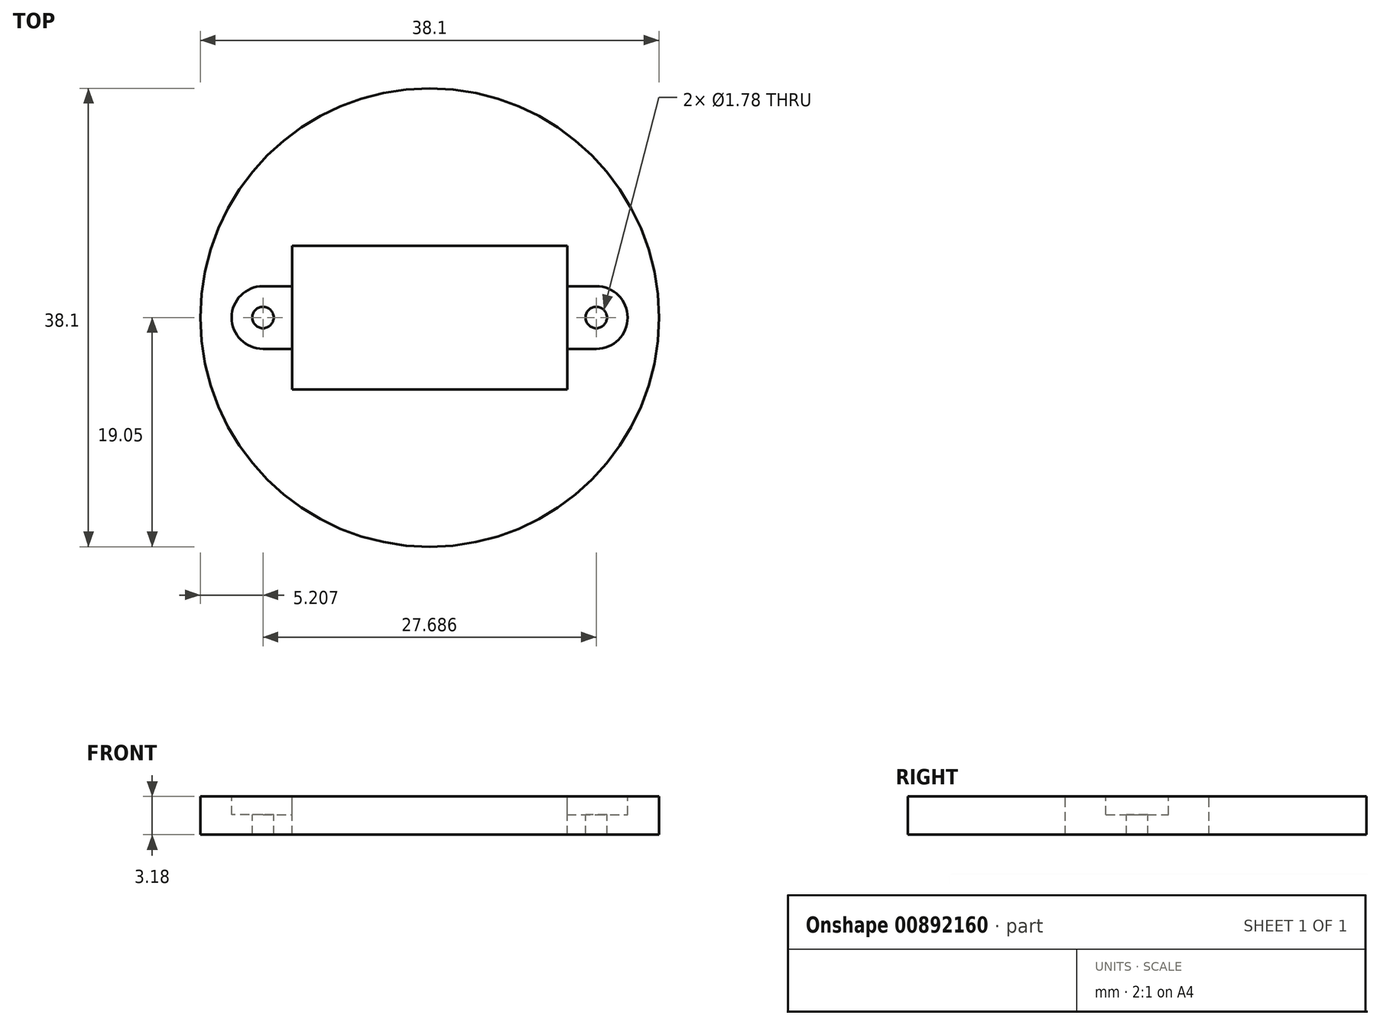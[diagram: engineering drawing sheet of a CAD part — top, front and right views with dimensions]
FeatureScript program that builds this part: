
annotation { "Feature Type Name" : "Feature", "Feature Type Description" : "" }
export const myFeature = defineFeature(function(context is Context, id is Id, definition is map)
    precondition{}
    {
        {
            var Q0;
            Q0=qCreatedBy(makeId("Top.planeOp"),FACE);
            var sketch = newSketch(context, id + "F0", { "sketchPlane" : qUnion([Q0])});
            skCircle(sketch, "E0", {"center": v(0, 0) * mm, "radius": 19.05 * mm});
            skSolve(sketch);
        }
        {
            var Q0;
            Q0=qSketchRegion(id+"F0",true);
            extrude(context, id + "F1", {"entities" : qUnion([Q0]), "depth" : 3.17 * mm, "offsetDistance" : 25.4 * mm});
        }
        {
            var Q0;
            Q0=makeQuery(id+"F1.opExtrude","CAP_FACE",FACE,{"disambiguationData":[OSD([sQuery(id+"F0.wireOp",EDGE,"E0")])],"isStart":false});
            var sketch = newSketch(context, id + "F2", { "sketchPlane" : qUnion([Q0])});
            skLineSegment(sketch, "E1.bottom", {"start": v(11.43, 5.97) * mm, "end": v(-11.43, 5.97) * mm});
            skLineSegment(sketch, "E1.top", {"start": v(11.43, -5.97) * mm, "end": v(-11.43, -5.97) * mm});
            skLineSegment(sketch, "E1.left", {"start": v(11.43, 5.97) * mm, "end": v(11.43, -5.97) * mm});
            skLineSegment(sketch, "E1.right", {"start": v(-11.43, 5.97) * mm, "end": v(-11.43, -5.97) * mm});
            skPoint(sketch, "E1.middle", {"position": v(0, 0) * mm});
            skCircle(sketch, "E2", {"center": v(-13.84, 0) * mm, "radius": 0.89 * mm});
            skCircle(sketch, "E3", {"center": v(13.84, 0) * mm, "radius": 0.89 * mm});
            skLineSegment(sketch, "E4", {"start": v(-13.84, 0) * mm, "end": v(13.84, 0) * mm, "construction": true});
            skSolve(sketch);
        }
        {
            var Q0;
            Q0 = qSketchRegion(id + "F2", true);
            extrude(context, id + "F3", {"entities" : qUnion([Q0]), "operationType" : NewBodyOperationType.REMOVE, "endBound" : BoundingType.THROUGH_ALL, "oppositeDirection" : true, "depth" : 25.4 * mm, "offsetDistance" : 25.4 * mm});
        }
        {
            var Q0;
            Q0=makeQuery(id+"F1.opExtrude","CAP_FACE",FACE,{"disambiguationData":[OSD([sQuery(id+"F0.wireOp",EDGE,"E0")])],"isStart":false});
            var sketch = newSketch(context, id + "F4", { "sketchPlane" : qUnion([Q0])});
            skArc(sketch, "E5", {"start": v(-13.84, 2.6) * mm, "mid": v(-16.45, 0) * mm, "end": v(-13.84, -2.6) * mm});
            skArc(sketch, "E6", {"start": v(13.84, -2.6) * mm, "mid": v(16.45, 0) * mm, "end": v(13.84, 2.6) * mm});
            skLineSegment(sketch, "E7.bottom", {"start": v(-13.84, -2.6) * mm, "end": v(13.84, -2.6) * mm});
            skLineSegment(sketch, "E7.top", {"start": v(-13.84, 2.6) * mm, "end": v(13.84, 2.6) * mm});
            skSolve(sketch);
        }
        {
            var Q0;
            Q0 = qSketchRegion(id + "F4", true);
            extrude(context, id + "F5", {"entities" : qUnion([Q0]), "operationType" : NewBodyOperationType.REMOVE, "oppositeDirection" : true, "depth" : 1.52 * mm, "offsetDistance" : 25.4 * mm});
        }
    });
